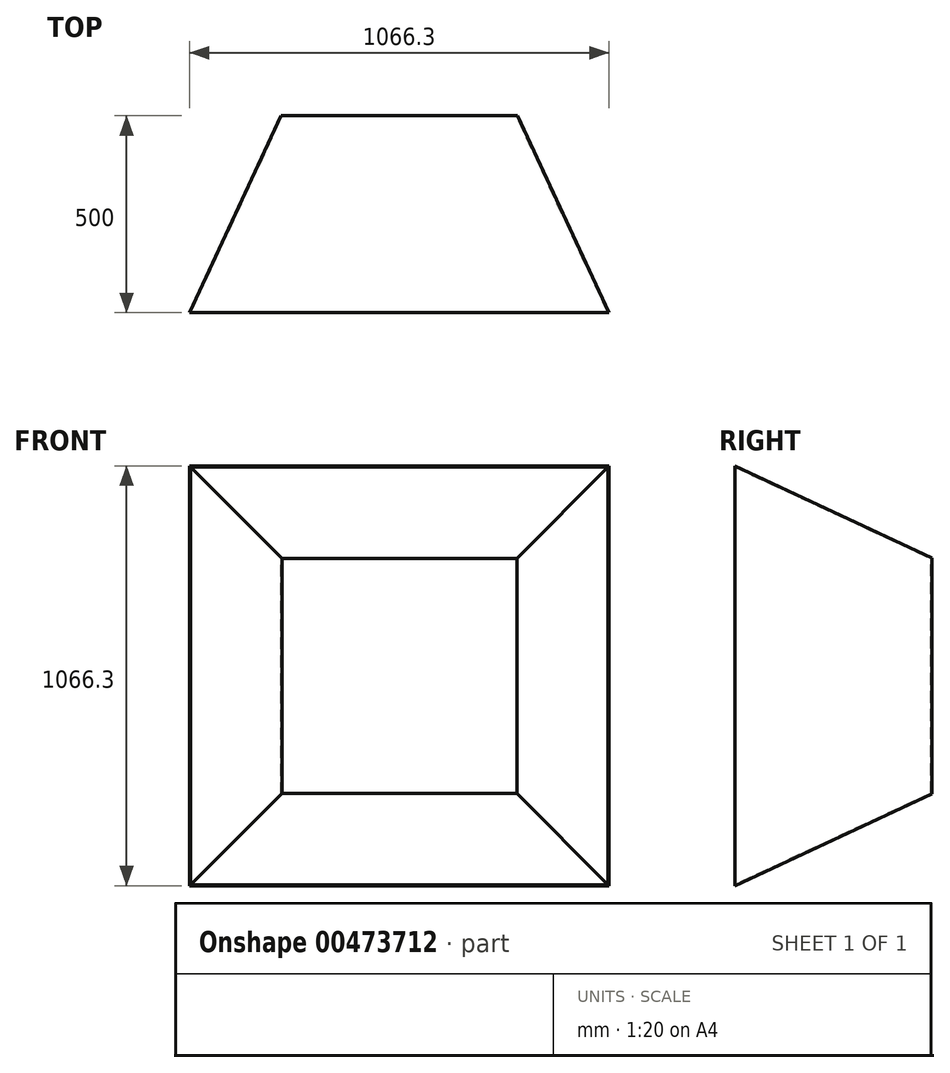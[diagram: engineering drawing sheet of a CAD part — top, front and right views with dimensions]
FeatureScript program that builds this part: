
annotation { "Feature Type Name" : "Feature", "Feature Type Description" : "" }
export const myFeature = defineFeature(function(context is Context, id is Id, definition is map)
    precondition{}
    {
        {
            var Q0;
            Q0=qCreatedBy(makeId("Front.planeOp"),FACE);
            var sketch = newSketch(context, id + "F0", { "sketchPlane" : qUnion([Q0])});
            skLineSegment(sketch, "E0.bottom", {"start": v(-300, -300) * mm, "end": v(300, -300) * mm});
            skLineSegment(sketch, "E0.top", {"start": v(-300, 300) * mm, "end": v(300, 300) * mm});
            skLineSegment(sketch, "E0.left", {"start": v(-300, -300) * mm, "end": v(-300, 300) * mm});
            skLineSegment(sketch, "E0.right", {"start": v(300, -300) * mm, "end": v(300, 300) * mm});
            skPoint(sketch, "E0.middle", {"position": v(0, 0) * mm});
            skSolve(sketch);
        }
        {
            var Q0;
            Q0=makeQuery(id+"F0.imprint","IMPRINT",FACE,{"disambiguationData":[TD([[makeQuery(id+"F0.imprint","IMPRINT",EDGE,{"derivedFrom":sQuery(id+"F0.wireOp",EDGE,"E0.bottom")}),1.0]])]});
            extrude(context, id + "F1", {"entities" : qUnion([Q0]), "depth" : 500 * mm, "hasDraft" : true, "draftAngle" : 25 * degree, "offsetDistance" : 25 * mm});
        }
        {
            var Q0;
            Q0=makeQuery(id+"F1.opExtrude","CAP_FACE",FACE,{"disambiguationData":[OSD([sQuery(id+"F0.wireOp",EDGE,"E0.bottom"),sQuery(id+"F0.wireOp",EDGE,"E0.top"),sQuery(id+"F0.wireOp",EDGE,"E0.left"),sQuery(id+"F0.wireOp",EDGE,"E0.right")])],"isStart":false});
            shell(context, id + "F2", {"entities" : qUnion([Q0]), "thickness" : 2.5 * mm});
        }
    });
